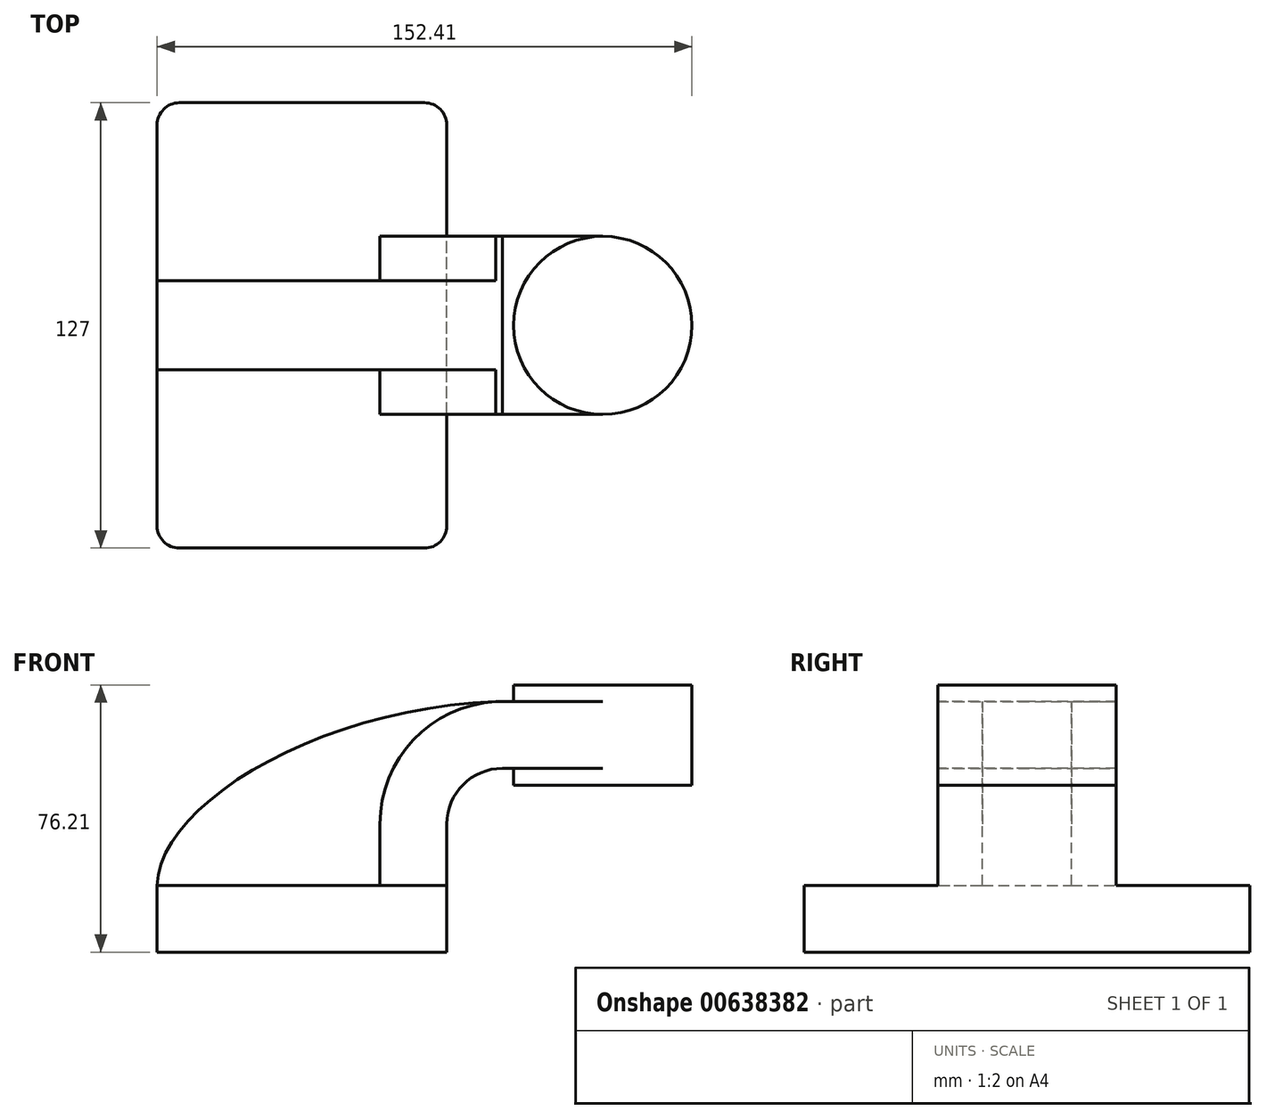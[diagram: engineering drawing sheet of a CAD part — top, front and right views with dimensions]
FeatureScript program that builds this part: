
annotation { "Feature Type Name" : "Feature", "Feature Type Description" : "" }
export const myFeature = defineFeature(function(context is Context, id is Id, definition is map)
    precondition{}
    {
        {
            var Q0;
            Q0=qCreatedBy(makeId("Front.planeOp"),FACE);
            var sketch = newSketch(context, id + "F0", { "sketchPlane" : qUnion([Q0])});
            skLineSegment(sketch, "E0.bottom", {"start": v(-41.28, 9.52) * mm, "end": v(41.27, 9.53) * mm});
            skLineSegment(sketch, "E0.top", {"start": v(-41.28, -9.53) * mm, "end": v(41.28, -9.53) * mm});
            skLineSegment(sketch, "E0.left", {"start": v(-41.28, 9.52) * mm, "end": v(-41.27, -9.53) * mm});
            skLineSegment(sketch, "E0.right", {"start": v(41.28, 9.53) * mm, "end": v(41.28, -9.52) * mm});
            skPoint(sketch, "E0.middle", {"position": v(0, 0) * mm});
            skLineSegment(sketch, "E1.bottom", {"start": v(60.32, 38.1) * mm, "end": v(111.12, 38.1) * mm});
            skLineSegment(sketch, "E1.top", {"start": v(60.32, 66.67) * mm, "end": v(111.12, 66.67) * mm});
            skLineSegment(sketch, "E1.left", {"start": v(60.32, 38.1) * mm, "end": v(60.32, 66.67) * mm});
            skLineSegment(sketch, "E1.right", {"start": v(111.12, 38.1) * mm, "end": v(111.12, 66.67) * mm});
            skPoint(sketch, "E1.middle", {"position": v(85.72, 52.39) * mm});
            skLineSegment(sketch, "E2", {"start": v(41.27, 9.53) * mm, "end": v(41.27, 27) * mm});
            skArc(sketch, "E3", {"start": v(41.27, 27) * mm, "mid": v(45.92, 38.23) * mm, "end": v(57.15, 42.88) * mm});
            skLineSegment(sketch, "E4", {"start": v(57.15, 42.88) * mm, "end": v(85.72, 42.88) * mm});
            skLineSegment(sketch, "E5.0", {"start": v(57.15, 61.93) * mm, "end": v(85.73, 61.93) * mm});
            skArc(sketch, "E5.1", {"start": v(22.23, 27) * mm, "mid": v(32.45, 51.7) * mm, "end": v(57.15, 61.93) * mm});
            skLineSegment(sketch, "E5.2", {"start": v(22.22, 9.53) * mm, "end": v(22.22, 27) * mm});
            skFitSpline(sketch, "E6", {"points": [v(-41.28, 9.52) * mm, v(57.15, 61.93) * mm], "startDerivative": vector(1.21, 69.88) * mm, "endDerivative": vector(153.57, 3.23) * mm});
            skLineSegment(sketch, "E7", {"start": v(85.72, 38.1) * mm, "end": v(85.72, 66.67) * mm});
            skSolve(sketch);
        }
        {
            var Q0;
            Q0=makeQuery(id+"F0.imprint","IMPRINT",FACE,{"disambiguationData":[TD([[makeQuery(id+"F0.imprint","IMPRINT",EDGE,{"derivedFrom":sQuery(id+"F0.wireOp",EDGE,"E0.top")}),1.0]])]});
            extrude(context, id + "F1", {"entities" : qUnion([Q0]), "endBound" : BoundingType.SYMMETRIC, "depth" : 127 * mm, "offsetDistance" : 25.4 * mm});
        }
        {
            var Q0;
            {var subQ1=sQuery(id+"F0.wireOp",EDGE,"E2");Q0=makeQuery(id+"F0.imprint","IMPRINT",FACE,{"disambiguationData":[TD([[makeQuery(id+"F0.imprint","IMPRINT",EDGE,{"derivedFrom":subQ1}),1.0]])]});}
            var Q1;
            {var subQ0=sQuery(id+"F0.wireOp",EDGE,"E4");var subQ1=sQuery(id+"F0.wireOp",EDGE,"E1.left");var subQ2=makeQuery(id+"F0.imprint","INTERSECT",VERTEX,{"derivedFrom":[subQ1,subQ0]});Q1=makeQuery(id+"F0.imprint","IMPRINT",FACE,{"disambiguationData":[TD([[makeQuery(id+"F0.imprint","IMPRINT",EDGE,{"disambiguationData":[TD([[subQ2,-1.0]])],"derivedFrom":subQ1}),-1.0]])]});}
            extrude(context, id + "F2", {"entities" : qUnion([Q0, Q1]), "operationType" : NewBodyOperationType.ADD, "endBound" : BoundingType.SYMMETRIC, "depth" : 50.8 * mm, "offsetDistance" : 25.4 * mm});
        }
        {
            var Q0;
            {var subQ3=sQuery(id+"F0.wireOp",EDGE,"E5.2");Q0=makeQuery(id+"F0.imprint","IMPRINT",FACE,{"disambiguationData":[TD([[makeQuery(id+"F0.imprint","IMPRINT",EDGE,{"derivedFrom":subQ3}),1.0]])]});}
            extrude(context, id + "F3", {"entities" : qUnion([Q0]), "operationType" : NewBodyOperationType.ADD, "endBound" : BoundingType.SYMMETRIC, "depth" : 25.4 * mm, "offsetDistance" : 25.4 * mm});
        }
        {
            var Q0;
            {var subQ4=sQuery(id+"F0.wireOp",EDGE,"E1.right");Q0=makeQuery(id+"F0.imprint","IMPRINT",FACE,{"disambiguationData":[TD([[makeQuery(id+"F0.imprint","IMPRINT",EDGE,{"derivedFrom":subQ4}),1.0]])]});}
            var Q1;
            Q1=sQuery(id+"F0.wireOp",EDGE,"E7");
            revolve(context, id + "F4", {"operationType" : NewBodyOperationType.ADD, "entities" : qUnion([Q0]), "axis" : qUnion([Q1]), "revolveType" : RevolveType.FULL});
        }
        {
            var Q0;
            Q0=makeQuery(id+"F1.opExtrude","CAP_EDGE",EDGE,{"disambiguationData":[OSD([sQuery(id+"F0.wireOp",EDGE,"E0.left")])],"isStart":false});
            var Q1;
            Q1=makeQuery(id+"F1.opExtrude","CAP_EDGE",EDGE,{"disambiguationData":[OSD([sQuery(id+"F0.wireOp",EDGE,"E0.right")])],"isStart":false});
            var Q2;
            Q2=makeQuery(id+"F1.opExtrude","CAP_EDGE",EDGE,{"disambiguationData":[OSD([sQuery(id+"F0.wireOp",EDGE,"E0.right")])],"isStart":true});
            var Q3;
            Q3=makeQuery(id+"F1.opExtrude","CAP_EDGE",EDGE,{"disambiguationData":[OSD([sQuery(id+"F0.wireOp",EDGE,"E0.left")])],"isStart":true});
            fillet(context, id + "F5", {"entities" : qUnion([Q0, Q1, Q2, Q3]), "radius" : 6.35 * mm, "tangentPropagation" : true, "allowEdgeOverflow" : false});
        }
    });
